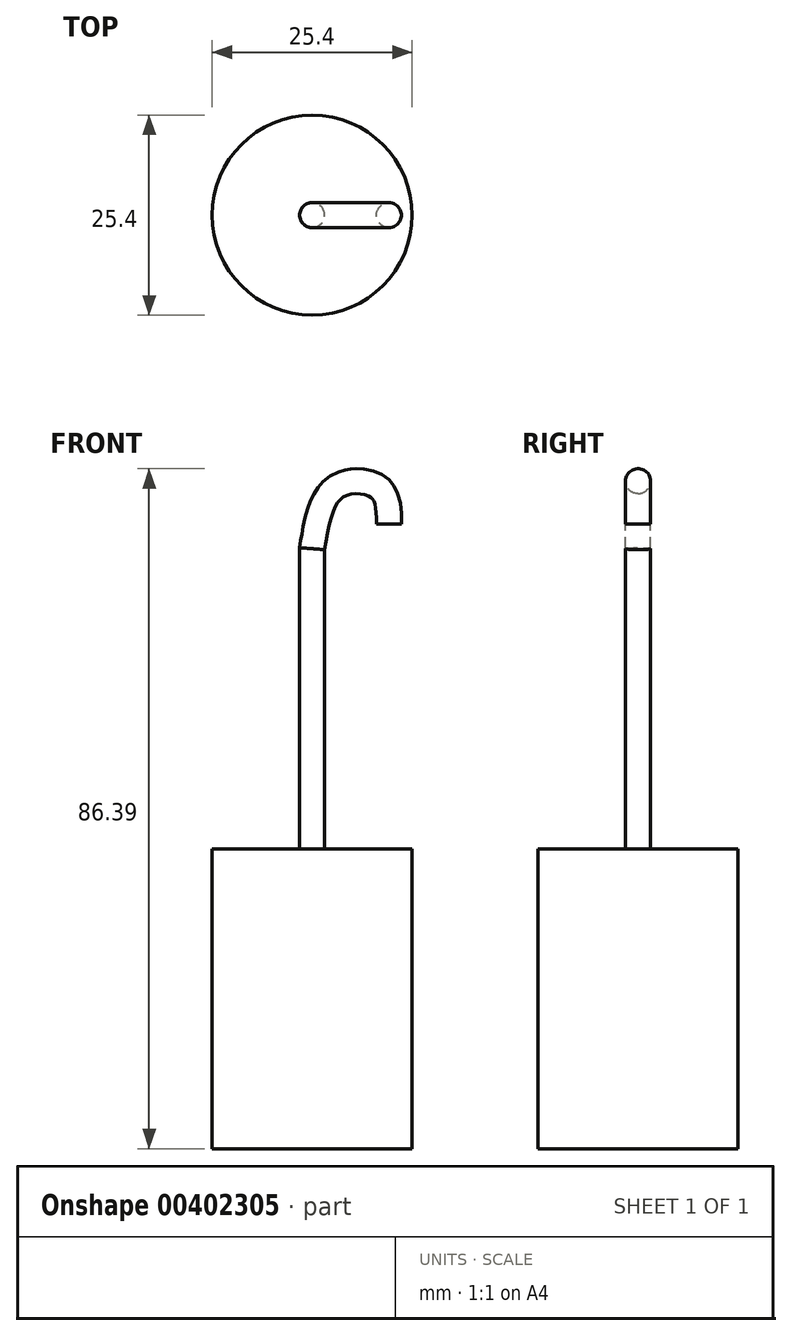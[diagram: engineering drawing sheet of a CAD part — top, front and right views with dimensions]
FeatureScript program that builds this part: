
annotation { "Feature Type Name" : "Feature", "Feature Type Description" : "" }
export const myFeature = defineFeature(function(context is Context, id is Id, definition is map)
    precondition{}
    {
        {
            var Q0;
            Q0=qCreatedBy(makeId("Top.planeOp"),FACE);
            var sketch = newSketch(context, id + "F0", { "sketchPlane" : qUnion([Q0])});
            skCircle(sketch, "E0", {"center": v(0, 0) * mm, "radius": 12.7 * mm});
            skSolve(sketch);
        }
        {
            var Q0;
            Q0 = qSketchRegion(id + "F0", true);
            extrude(context, id + "F1", {"entities" : qUnion([Q0]), "depth" : 38.1 * mm, "symmetric" : true});
        }
        {
            var Q0;
            Q0=makeQuery(id+"F1.opExtrude","CAP_FACE",FACE,{"disambiguationData":[OSD([sQuery(id+"F0.wireOp",EDGE,"E0")])],"isStart":false});
            var sketch = newSketch(context, id + "F2", { "sketchPlane" : qUnion([Q0])});
            skCircle(sketch, "E1", {"center": v(0, 0) * mm, "radius": 1.59 * mm});
            skSolve(sketch);
        }
        {
            var Q0;
            Q0=qCreatedBy(makeId("Front.planeOp"),FACE);
            var sketch = newSketch(context, id + "F3", { "sketchPlane" : qUnion([Q0])});
            skLineSegment(sketch, "E2", {"start": v(0, 19.07) * mm, "end": v(0, 57.17) * mm});
            skFitSpline(sketch, "E3", {"points": [v(0, 57.17) * mm, v(3.06, 65.03) * mm, v(8.57, 64.84) * mm, v(9.76, 60.26) * mm], "startDerivative": vector(3.97, 25.02) * mm, "endDerivative": vector(0.07, -18.28) * mm});
            skSolve(sketch);
        }
        {
            var Q0;
            Q0 = qSketchRegion(id + "F2", true);
            var Q1;
            Q1 = qConstructionFilter(qBodyType(qCreatedBy(id + "F3" ,EDGE), BodyType.WIRE), ConstructionObject.NO);
            sweep(context, id + "F4", {"operationType" : NewBodyOperationType.ADD, "profiles" : qUnion([Q0]), "path" : qUnion([Q1])});
        }
    });
